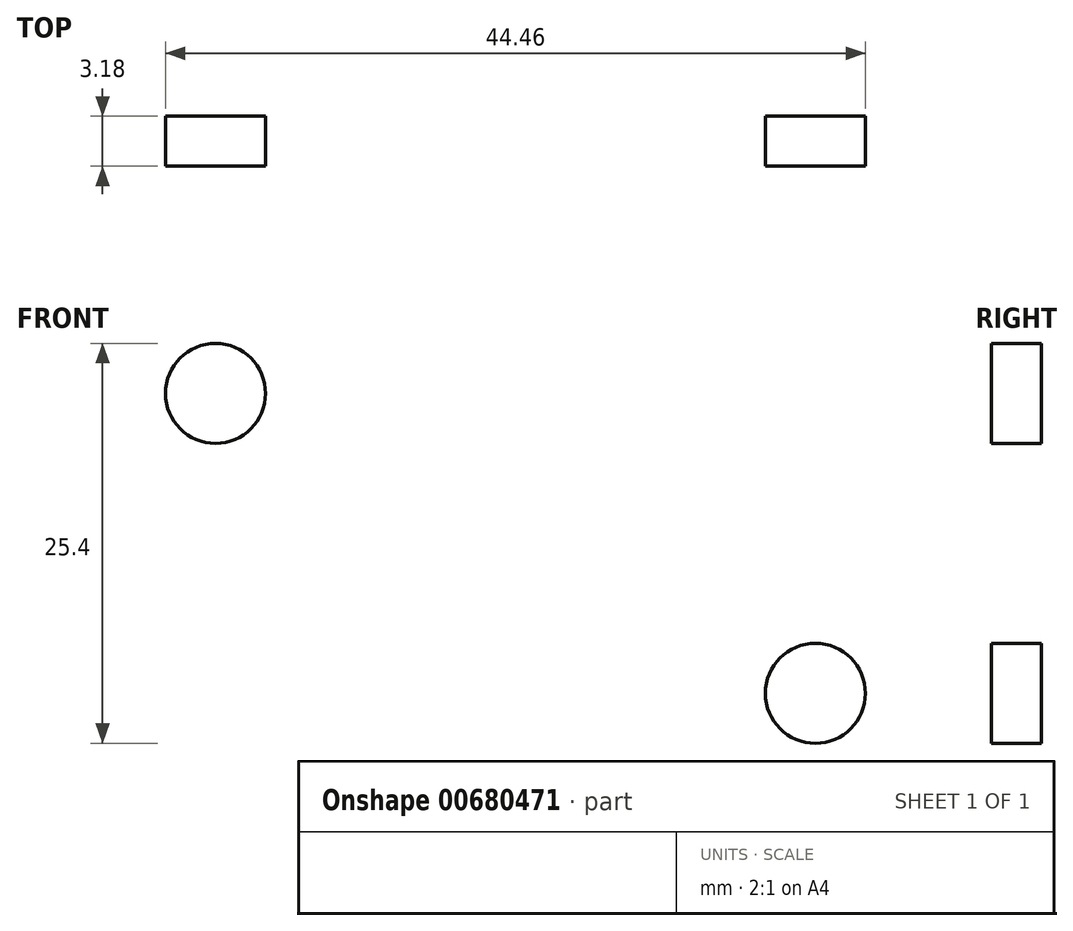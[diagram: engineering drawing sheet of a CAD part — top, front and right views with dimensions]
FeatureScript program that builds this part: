
annotation { "Feature Type Name" : "Feature", "Feature Type Description" : "" }
export const myFeature = defineFeature(function(context is Context, id is Id, definition is map)
    precondition{}
    {
        {
            var Q0;
            Q0=qCreatedBy(makeId("Front.planeOp"),FACE);
            var sketch = newSketch(context, id + "F0", { "sketchPlane" : qUnion([Q0])});
            skCircle(sketch, "E0", {"center": v(0, 0) * mm, "radius": 4.76 * mm});
            skCircle(sketch, "E1", {"center": v(-26.04, 0) * mm, "radius": 1.98 * mm});
            skLineSegment(sketch, "E2", {"start": v(-26.04, 0) * mm, "end": v(26.04, 0) * mm, "construction": true});
            skCircle(sketch, "E3", {"center": v(26.04, 0) * mm, "radius": 1.98 * mm});
            skLineSegment(sketch, "E4.bottom", {"start": v(-38.1, 25.4) * mm, "end": v(38.1, 25.4) * mm});
            skLineSegment(sketch, "E4.top", {"start": v(-38.1, -114.3) * mm, "end": v(38.1, -114.3) * mm});
            skLineSegment(sketch, "E4.left", {"start": v(-38.1, 25.4) * mm, "end": v(-38.1, -114.3) * mm});
            skLineSegment(sketch, "E4.right", {"start": v(38.1, 25.4) * mm, "end": v(38.1, -114.3) * mm});
            skLineSegment(sketch, "E5", {"start": v(0, 0) * mm, "end": v(0, 25.4) * mm, "construction": true});
            skSolve(sketch);
        }
        {
            var Q0;
            Q0=makeQuery(id+"F0.imprint","IMPRINT",FACE,{"disambiguationData":[TD([[makeQuery(id+"F0.imprint","IMPRINT",EDGE,{"derivedFrom":sQuery(id+"F0.wireOp",EDGE,"E0")}),-1.0]])]});
            extrude(context, id + "F1", {"entities" : qUnion([Q0]), "depth" : 3.17 * mm, "offsetDistance" : 25.4 * mm});
        }
        {
            var Q0;
            Q0=makeQuery(id+"F1.opExtrude","CAP_FACE",FACE,{"disambiguationData":[OSD([sQuery(id+"F0.wireOp",EDGE,"E0"),sQuery(id+"F0.wireOp",EDGE,"E1"),sQuery(id+"F0.wireOp",EDGE,"E3"),sQuery(id+"F0.wireOp",EDGE,"E4.bottom"),sQuery(id+"F0.wireOp",EDGE,"E4.top"),sQuery(id+"F0.wireOp",EDGE,"E4.left"),sQuery(id+"F0.wireOp",EDGE,"E4.right")])],"isStart":false});
            var sketch = newSketch(context, id + "F2", { "sketchPlane" : qUnion([Q0])});
            skLineSegment(sketch, "E6", {"start": v(38.1, -95.25) * mm, "end": v(-38.1, -95.25) * mm, "construction": true});
            skCircle(sketch, "E7", {"center": v(-19.05, -104.78) * mm, "radius": 3.18 * mm});
            skLineSegment(sketch, "E8", {"start": v(-19.05, -95.25) * mm, "end": v(-19.05, -114.3) * mm, "construction": true});
            skLineSegment(sketch, "E9", {"start": v(0, -114.3) * mm, "end": v(-38.1, -114.3) * mm, "construction": true});
            skLineSegment(sketch, "E10", {"start": v(0, -114.3) * mm, "end": v(0, 25.4) * mm, "construction": true});
            skCircle(sketch, "E11.MirrorC", {"center": v(-19.05, -85.73) * mm, "radius": 3.18 * mm});
            skCircle(sketch, "E12.MirrorC", {"center": v(19.05, -85.73) * mm, "radius": 3.18 * mm});
            skCircle(sketch, "E13.MirrorC", {"center": v(19.05, -104.78) * mm, "radius": 3.18 * mm});
            skSolve(sketch);
        }
        {
            var Q0;
            Q0=makeQuery(id+"F2.imprint","IMPRINT",FACE,{"disambiguationData":[TD([[makeQuery(id+"F2.imprint","IMPRINT",EDGE,{"derivedFrom":sQuery(id+"F2.wireOp",EDGE,"E12.MirrorC")}),1.0]])]});
            var Q1;
            Q1=makeQuery(id+"F2.imprint","IMPRINT",FACE,{"disambiguationData":[TD([[makeQuery(id+"F2.imprint","IMPRINT",EDGE,{"derivedFrom":sQuery(id+"F2.wireOp",EDGE,"E13.MirrorC")}),-1.0]])]});
            var Q2;
            Q2=makeQuery(id+"F2.imprint","IMPRINT",FACE,{"disambiguationData":[TD([[makeQuery(id+"F2.imprint","IMPRINT",EDGE,{"derivedFrom":sQuery(id+"F2.wireOp",EDGE,"E11.MirrorC")}),-1.0]])]});
            var Q3;
            Q3=makeQuery(id+"F2.imprint","IMPRINT",FACE,{"disambiguationData":[TD([[makeQuery(id+"F2.imprint","IMPRINT",EDGE,{"derivedFrom":sQuery(id+"F2.wireOp",EDGE,"E7")}),1.0]])]});
            extrude(context, id + "F3", {"entities" : qUnion([Q0, Q1, Q2, Q3]), "operationType" : NewBodyOperationType.REMOVE, "endBound" : BoundingType.THROUGH_ALL, "oppositeDirection" : true, "depth" : 25.4 * mm, "offsetDistance" : 25.4 * mm});
        }
    });
